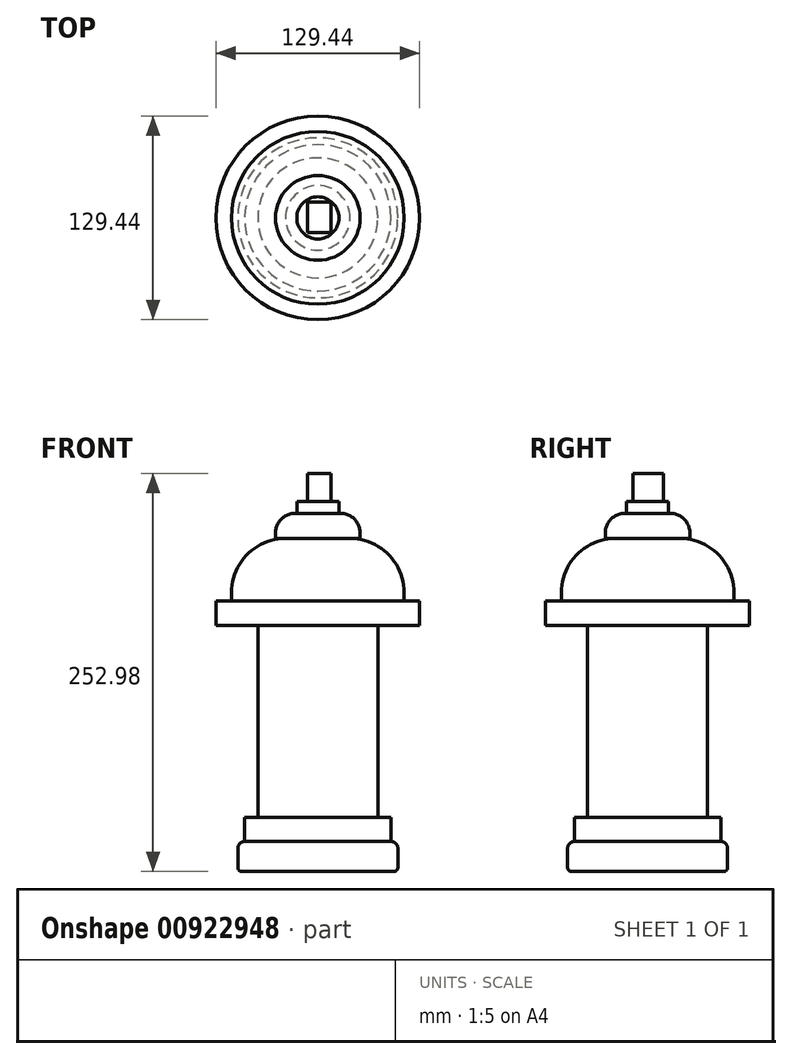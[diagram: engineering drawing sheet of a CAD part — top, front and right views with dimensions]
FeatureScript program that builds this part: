
annotation { "Feature Type Name" : "Feature", "Feature Type Description" : "" }
export const myFeature = defineFeature(function(context is Context, id is Id, definition is map)
    precondition{}
    {
        {
            var Q0;
            Q0=qCreatedBy(makeId("Top.planeOp"),FACE);
            var sketch = newSketch(context, id + "F0", { "sketchPlane" : qUnion([Q0])});
            skCircle(sketch, "E0", {"center": v(0, 0) * mm, "radius": 50.8 * mm});
            skSolve(sketch);
        }
        {
            var Q0;
            Q0=makeQuery(id+"F0.imprint","IMPRINT",FACE,{"disambiguationData":[TD([[makeQuery(id+"F0.imprint","IMPRINT",EDGE,{"derivedFrom":sQuery(id+"F0.wireOp",EDGE,"E0")}),1.0]])]});
            extrude(context, id + "F1", {"entities" : qUnion([Q0]), "depth" : 19.05 * mm, "offsetDistance" : 25.4 * mm});
        }
        {
            var Q0;
            Q0=makeQuery(id+"F1.opExtrude","CAP_EDGE",EDGE,{"disambiguationData":[OSD([sQuery(id+"F0.wireOp",EDGE,"E0")])],"isStart":false});
            fillet(context, id + "F2", {"entities" : qUnion([Q0]), "radius" : 4.32 * mm, "tangentPropagation" : true, "allowEdgeOverflow" : false});
        }
        {
            var Q0;
            Q0=makeQuery(id+"F1.opExtrude","CAP_EDGE",EDGE,{"disambiguationData":[OSD([sQuery(id+"F0.wireOp",EDGE,"E0")])],"isStart":true});
            fillet(context, id + "F3", {"entities" : qUnion([Q0]), "radius" : 2.54 * mm, "tangentPropagation" : true, "allowEdgeOverflow" : false});
        }
        {
            var Q0;
            Q0=makeQuery(id+"F1.opExtrude","CAP_FACE",FACE,{"disambiguationData":[OSD([sQuery(id+"F0.wireOp",EDGE,"E0")])],"isStart":false});
            cPlane(context, id + "F4", {"entities" : qUnion([Q0]), "cplaneType" : CPlaneType.OFFSET, "offset" : 0 * mm, "width" : 152.4 * mm, "height" : 152.4 * mm});
        }
        {
            var Q0;
            Q0=qCreatedBy(id+"F4.planeOp",FACE);
            var sketch = newSketch(context, id + "F5", { "sketchPlane" : qUnion([Q0])});
            skCircle(sketch, "E1", {"center": v(0, 0) * mm, "radius": 38.1 * mm});
            skSolve(sketch);
        }
        {
            var Q0;
            Q0 = qSketchRegion(id + "F5", true);
            extrude(context, id + "F6", {"entities" : qUnion([Q0]), "operationType" : NewBodyOperationType.ADD, "depth" : 137.4 * mm, "offsetDistance" : 25.4 * mm});
        }
        {
            var Q0;
            Q0=makeQuery(id+"F6.opExtrude","CAP_FACE",FACE,{"disambiguationData":[OSD([sQuery(id+"F5.wireOp",EDGE,"E1")])],"isStart":false});
            cPlane(context, id + "F7", {"entities" : qUnion([Q0]), "cplaneType" : CPlaneType.OFFSET, "offset" : 0 * mm, "width" : 152.4 * mm, "height" : 152.4 * mm});
        }
        {
            var Q0;
            Q0=qCreatedBy(id+"F7.planeOp",FACE);
            var sketch = newSketch(context, id + "F8", { "sketchPlane" : qUnion([Q0])});
            skCircle(sketch, "E2", {"center": v(0, 0) * mm, "radius": 64.72 * mm});
            skSolve(sketch);
        }
        {
            var Q0;
            Q0 = qSketchRegion(id + "F8", true);
            var Q1;
            Q1=makeQuery(id+"F1.opExtrude","CAP_FACE",FACE,{"disambiguationData":[OSD([sQuery(id+"F0.wireOp",EDGE,"E0")])],"isStart":false});
            extrude(context, id + "F9", {"entities" : qUnion([Q0, Q1]), "operationType" : NewBodyOperationType.ADD, "depth" : 15.5 * mm, "offsetDistance" : 25.4 * mm});
        }
        {
            var Q0;
            Q0=makeQuery(id+"F9.opExtrude","CAP_FACE",FACE,{"disambiguationData":[OSD([sQuery(id+"F8.wireOp",EDGE,"E2")])],"isStart":false});
            cPlane(context, id + "F10", {"entities" : qUnion([Q0]), "cplaneType" : CPlaneType.OFFSET, "offset" : 0 * mm, "width" : 152.4 * mm, "height" : 152.4 * mm});
        }
        {
            var Q0;
            Q0=qCreatedBy(id+"F10.planeOp",FACE);
            var sketch = newSketch(context, id + "F11", { "sketchPlane" : qUnion([Q0])});
            skCircle(sketch, "E3", {"center": v(0, 0) * mm, "radius": 54.83 * mm});
            skSolve(sketch);
        }
        {
            var Q0;
            Q0 = qSketchRegion(id + "F11", true);
            extrude(context, id + "F12", {"entities" : qUnion([Q0]), "operationType" : NewBodyOperationType.ADD, "depth" : 39.62 * mm, "offsetDistance" : 25.4 * mm});
        }
        {
            var Q0;
            Q0=makeQuery(id+"F12.opExtrude","CAP_EDGE",EDGE,{"disambiguationData":[OSD([sQuery(id+"F11.wireOp",EDGE,"E3")])],"isStart":false});
            fillet(context, id + "F13", {"entities" : qUnion([Q0]), "radius" : 34.34 * mm, "tangentPropagation" : true, "allowEdgeOverflow" : false});
        }
        {
            var Q0;
            Q0=makeQuery(id+"F12.opExtrude","CAP_FACE",FACE,{"disambiguationData":[OSD([sQuery(id+"F11.wireOp",EDGE,"E3")])],"isStart":false});
            cPlane(context, id + "F14", {"entities" : qUnion([Q0]), "cplaneType" : CPlaneType.OFFSET, "offset" : 0 * mm, "width" : 152.4 * mm, "height" : 152.4 * mm});
        }
        {
            var Q0;
            Q0=qCreatedBy(id+"F14.planeOp",FACE);
            var sketch = newSketch(context, id + "F15", { "sketchPlane" : qUnion([Q0])});
            skCircle(sketch, "E4", {"center": v(0, 0) * mm, "radius": 26.88 * mm});
            skSolve(sketch);
        }
        {
            var Q0;
            Q0=makeQuery(id+"F15.imprint","IMPRINT",FACE,{"disambiguationData":[TD([[makeQuery(id+"F15.imprint","IMPRINT",EDGE,{"derivedFrom":sQuery(id+"F15.wireOp",EDGE,"E4")}),1.0]])]});
            extrude(context, id + "F16", {"entities" : qUnion([Q0]), "operationType" : NewBodyOperationType.ADD, "depth" : 16 * mm, "offsetDistance" : 25.4 * mm});
        }
        {
            var Q0;
            Q0=makeQuery(id+"F16.opExtrude","CAP_EDGE",EDGE,{"disambiguationData":[OSD([sQuery(id+"F15.wireOp",EDGE,"E4")])],"isStart":false});
            fillet(context, id + "F17", {"entities" : qUnion([Q0]), "radius" : 12.7 * mm, "tangentPropagation" : true, "allowEdgeOverflow" : false});
        }
        {
            var Q0;
            Q0=makeQuery(id+"F16.opExtrude","CAP_FACE",FACE,{"disambiguationData":[OSD([sQuery(id+"F15.wireOp",EDGE,"E4")])],"isStart":false});
            cPlane(context, id + "F18", {"entities" : qUnion([Q0]), "cplaneType" : CPlaneType.OFFSET, "offset" : 0 * mm, "width" : 152.4 * mm, "height" : 152.4 * mm});
        }
        {
            var Q0;
            Q0=qCreatedBy(id+"F18.planeOp",FACE);
            var sketch = newSketch(context, id + "F19", { "sketchPlane" : qUnion([Q0])});
            skCircle(sketch, "E5", {"center": v(0, 0) * mm, "radius": 13.38 * mm});
            skSolve(sketch);
        }
        {
            var Q0;
            Q0=makeQuery(id+"F19.imprint","IMPRINT",FACE,{"disambiguationData":[TD([[makeQuery(id+"F19.imprint","IMPRINT",EDGE,{"derivedFrom":sQuery(id+"F19.wireOp",EDGE,"E5")}),1.0]])]});
            extrude(context, id + "F20", {"entities" : qUnion([Q0]), "operationType" : NewBodyOperationType.ADD, "depth" : 7.62 * mm, "offsetDistance" : 25.4 * mm});
        }
        {
            var Q0;
            Q0=makeQuery(id+"F20.opExtrude","CAP_FACE",FACE,{"disambiguationData":[OSD([sQuery(id+"F19.wireOp",EDGE,"E5")])],"isStart":false});
            cPlane(context, id + "F21", {"entities" : qUnion([Q0]), "cplaneType" : CPlaneType.OFFSET, "offset" : 0 * mm, "width" : 152.4 * mm, "height" : 152.4 * mm});
        }
        {
            var Q0;
            Q0=qCreatedBy(id+"F21.planeOp",FACE);
            var sketch = newSketch(context, id + "F22", { "sketchPlane" : qUnion([Q0])});
            skLineSegment(sketch, "E6.bottom", {"start": v(-6.57, 10.17) * mm, "end": v(8.43, 10.17) * mm});
            skLineSegment(sketch, "E6.top", {"start": v(-6.57, -9.46) * mm, "end": v(8.43, -9.46) * mm});
            skLineSegment(sketch, "E6.left", {"start": v(-6.57, 10.17) * mm, "end": v(-6.57, -9.46) * mm});
            skLineSegment(sketch, "E6.right", {"start": v(8.43, 10.17) * mm, "end": v(8.43, -9.46) * mm});
            skSolve(sketch);
        }
        {
            var Q0;
            Q0=makeQuery(id+"F22.imprint","IMPRINT",FACE,{"disambiguationData":[TD([[makeQuery(id+"F22.imprint","IMPRINT",EDGE,{"derivedFrom":sQuery(id+"F22.wireOp",EDGE,"E6.bottom")}),-1.0]])]});
            extrude(context, id + "F23", {"entities" : qUnion([Q0]), "operationType" : NewBodyOperationType.ADD, "depth" : 17.78 * mm, "offsetDistance" : 25.4 * mm});
        }
    });
